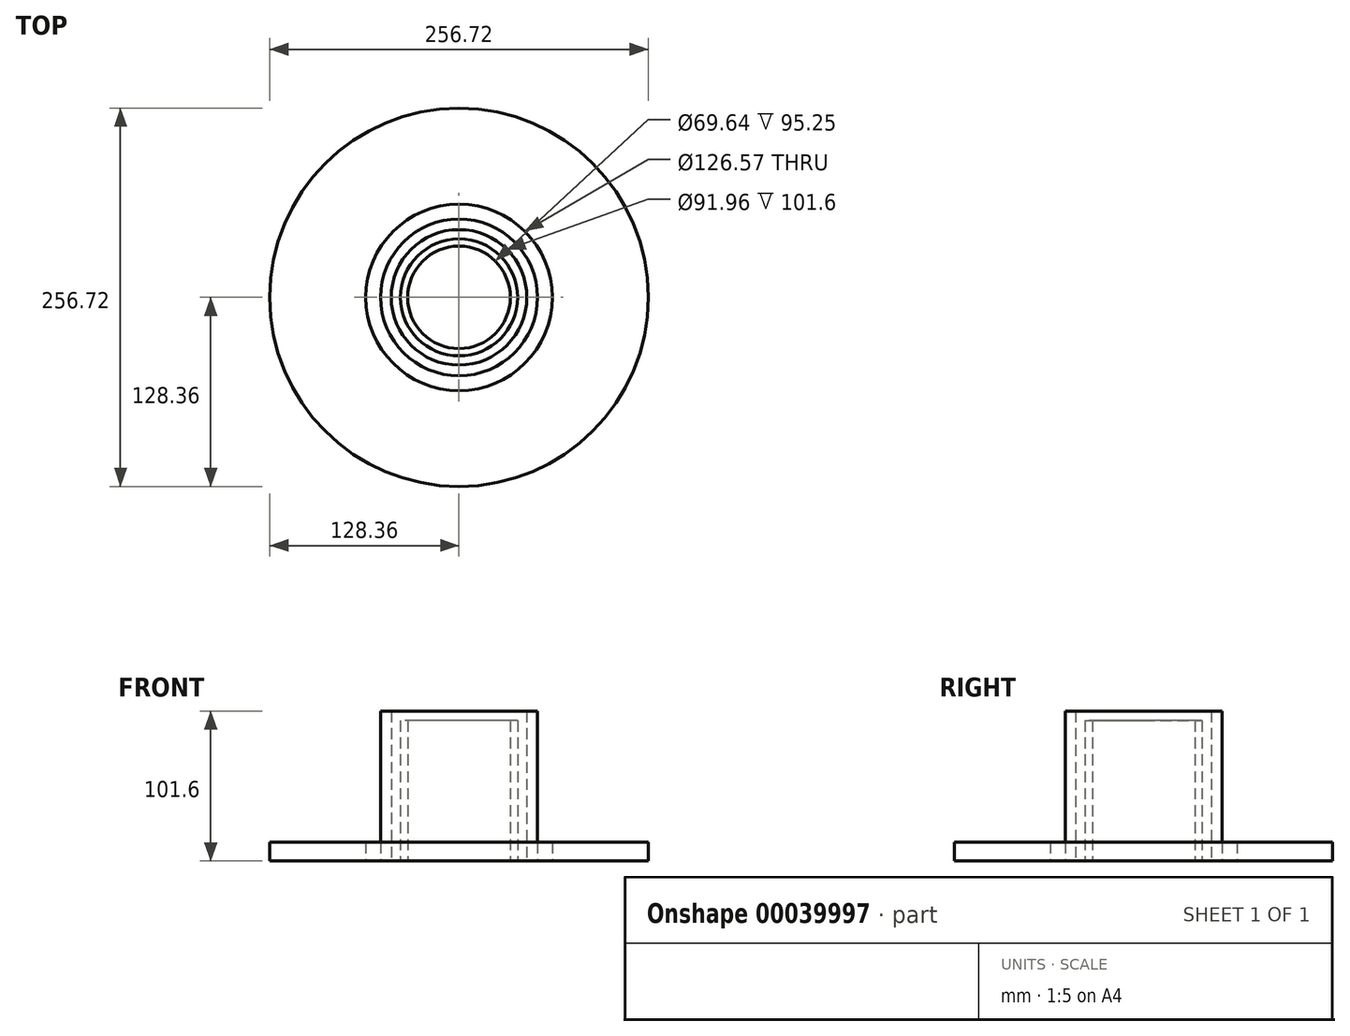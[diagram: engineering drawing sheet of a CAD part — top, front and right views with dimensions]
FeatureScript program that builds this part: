
annotation { "Feature Type Name" : "Feature", "Feature Type Description" : "" }
export const myFeature = defineFeature(function(context is Context, id is Id, definition is map)
    precondition{}
    {
        {
            var Q0;
            Q0=qCreatedBy(makeId("Top.planeOp"),FACE);
            var sketch = newSketch(context, id + "F0", { "sketchPlane" : qUnion([Q0])});
            skCircle(sketch, "E0", {"center": v(0, 0) * mm, "radius": 45.98 * mm});
            skCircle(sketch, "E1", {"center": v(0, 0) * mm, "radius": 53.2 * mm});
            skSolve(sketch);
        }
        {
            var Q0;
            Q0=makeQuery(id+"F0.imprint","IMPRINT",FACE,{"disambiguationData":[TD([[makeQuery(id+"F0.imprint","IMPRINT",EDGE,{"derivedFrom":sQuery(id+"F0.wireOp",EDGE,"E0")}),-1.0]])]});
            extrude(context, id + "F1", {"entities" : qUnion([Q0]), "depth" : 101.6 * mm});
        }
        {
            var Q0;
            Q0=sQuery(id+"F0.wireOp",EDGE,"E0");
            extrude(context, id + "F2", {"bodyType" : ToolBodyType.SURFACE, "surfaceEntities" : qUnion([Q0]), "depth" : 101.6 * mm});
        }
        {
            var Q0;
            Q0=qCreatedBy(makeId("Top.planeOp"),FACE);
            var sketch = newSketch(context, id + "F3", { "sketchPlane" : qUnion([Q0])});
            skCircle(sketch, "E2", {"center": v(0, 0) * mm, "radius": 39.71 * mm});
            skCircle(sketch, "E3", {"center": v(0, 0) * mm, "radius": 34.82 * mm});
            skSolve(sketch);
        }
        {
            var Q0;
            Q0 = qSketchRegion(id + "F3", true);
            var Q1;
            Q1=makeQuery(id+"F3.imprint","IMPRINT",FACE,{"disambiguationData":[TD([[makeQuery(id+"F3.imprint","IMPRINT",EDGE,{"derivedFrom":sQuery(id+"F3.wireOp",EDGE,"E2")}),1.0]])]});
            extrude(context, id + "F4", {"entities" : qUnion([Q0, Q1]), "depth" : 95.25 * mm});
        }
        {
            var Q0;
            Q0=qCreatedBy(makeId("Top.planeOp"),FACE);
            var sketch = newSketch(context, id + "F5", { "sketchPlane" : qUnion([Q0])});
            skCircle(sketch, "E4", {"center": v(0, 0) * mm, "radius": 128.36 * mm});
            skCircle(sketch, "E5", {"center": v(0, 0) * mm, "radius": 57.26 * mm});
            skCircle(sketch, "E6.0", {"center": v(0, 0) * mm, "radius": 63.28 * mm});
            skSolve(sketch);
        }
        {
            var Q0;
            Q0=makeQuery(id+"F5.imprint","IMPRINT",FACE,{"disambiguationData":[TD([[makeQuery(id+"F5.imprint","IMPRINT",EDGE,{"derivedFrom":sQuery(id+"F5.wireOp",EDGE,"E4")}),1.0]])]});
            extrude(context, id + "F6", {"entities" : qUnion([Q0]), "depth" : 12.7 * mm});
        }
    });
